# Revit family: Hekatron_Rauchwarnmelder_Genius Port_DE_22.01
name_source: partatom
category: Brandmelder
revit_build: Autodesk Revit 2018 (Build: 20190510_1515(x64)
units: mm (PartAtom-declared; Revit-internal decimal feet)

## family parameters
Basisbauteil = Fläche
Beim Laden mit Abzugskörper schneiden = Nein
Bemaßung runder Anschluss = Durchmesser verwenden
Beschriftungsausrichtung beibehalten = Ja
Gemeinsam genutzt = Nein
OmniClass-Nummer = 23.85.30.21
OmniClass-Titel = Environmental Detection/Registration
Raumberechnungspunkt = Nein
Teiletyp = Normal

## types (1)
- Genius Port
    Beschreibung = Genius Port zur Vernetzung und Bedienung des Genius Funknetzwerks für zusätzliche Funktionalitäten und Services.
    Betriebsspannung = 5 V DC über Steckernetzteil
    Breite (mm) = 160.0
    Farbe = RAL 9003 / RAL 9005
    Funktionsprinzip = Funk, LAN/W-LAN
    Hersteller = Hekatron
    Höhe (mm) = 130.0
    Kabeleinführung = seitlich
    Link zu Ausschreibungstext = https://www.meinhplus.de
    Link zu ausschreiben.de = https://www.ausschreiben.de
    Link zum Datenblatt = https://www.hekatron-planungstools.de
    Material = PC-ABS/POM
    Modell = Genius Port
    Montageart = Aufputz
    Nettogewicht (g) = 250.0
    Schutzart = IP 20
    Tiefe (mm) = 25.0
    Typenkommentare = Genius Port für Funksystem Genius
    UB A&S Artikel Nummer = 31-6000001-01-01
    URL = https://www.hekatron-brandschutz.de
    Version des BIM Objektes = 22.01
    Vorgabe-Ansicht = 1200 mm
    Zulässige Umgebungstemperatur = 0 °C bis + 55 °C

## geometry (parser evidence)
native form markers: Sweep x2
no freeform markers — native parametric forms only
